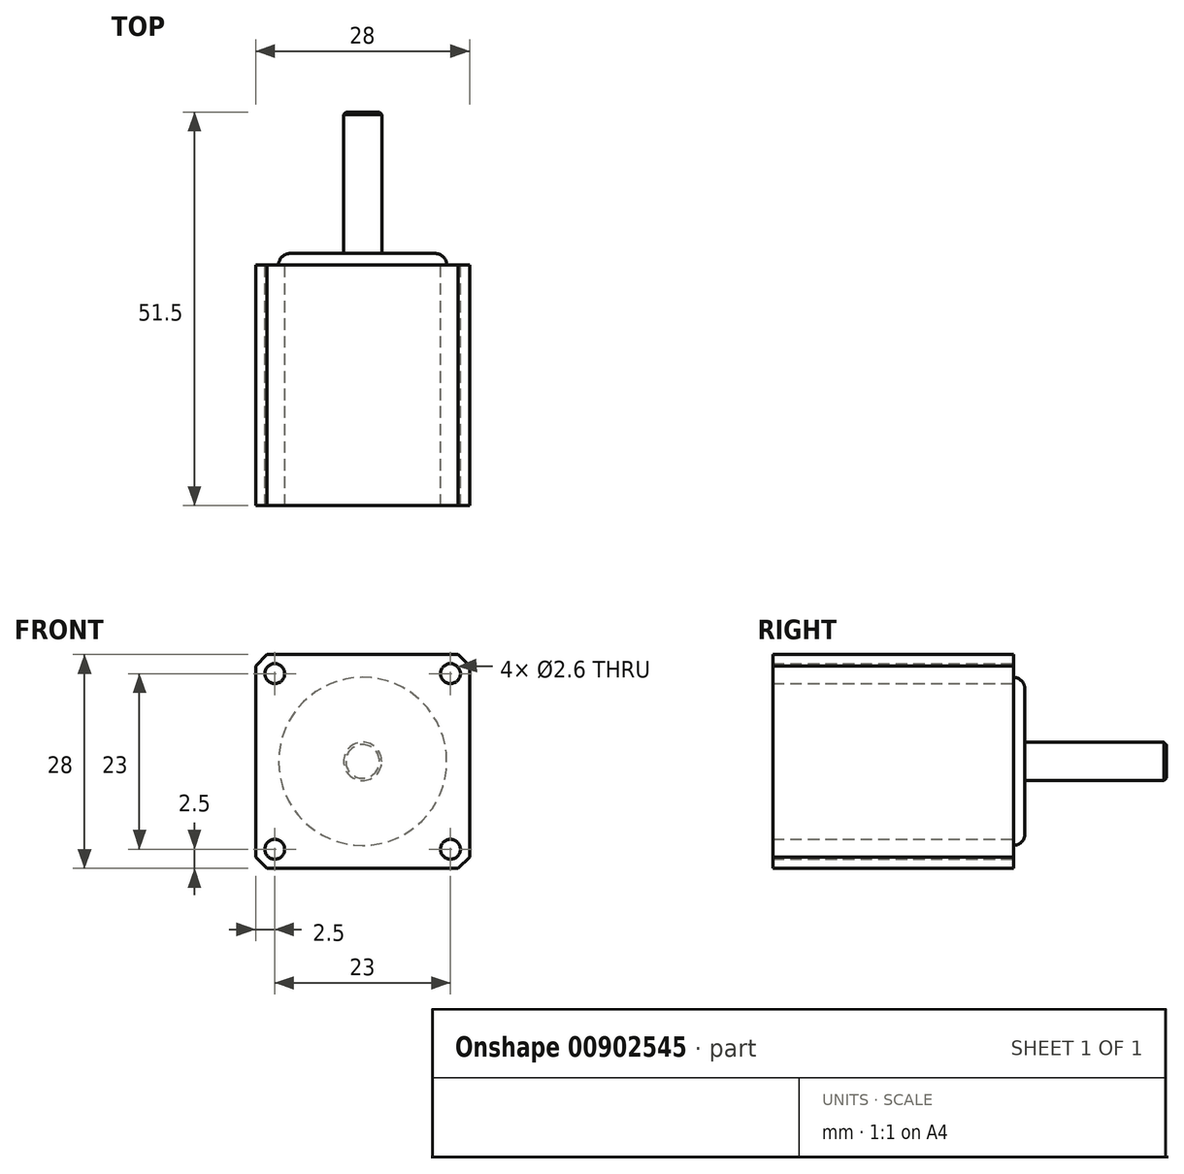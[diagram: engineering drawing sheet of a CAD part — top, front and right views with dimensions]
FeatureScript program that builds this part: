
annotation { "Feature Type Name" : "Feature", "Feature Type Description" : "" }
export const myFeature = defineFeature(function(context is Context, id is Id, definition is map)
    precondition{}
    {
        {
            var Q0;
            Q0=qCreatedBy(makeId("Front.planeOp"),FACE);
            var sketch = newSketch(context, id + "F0", { "sketchPlane" : qUnion([Q0])});
            skPoint(sketch, "E0.middle", {"position": v(0, 0) * mm});
            skLineSegment(sketch, "E1.bottom", {"start": v(14, 14) * mm, "end": v(-14, 14) * mm});
            skLineSegment(sketch, "E1.top", {"start": v(14, -14) * mm, "end": v(-14, -14) * mm});
            skLineSegment(sketch, "E1.left", {"start": v(14, 14) * mm, "end": v(14, -14) * mm});
            skLineSegment(sketch, "E1.right", {"start": v(-14, 14) * mm, "end": v(-14, -14) * mm});
            skSolve(sketch);
        }
        {
            var Q0;
            Q0=makeQuery(id+"F0.imprint","IMPRINT",FACE,{"disambiguationData":[TD([[makeQuery(id+"F0.imprint","IMPRINT",EDGE,{"derivedFrom":sQuery(id+"F0.wireOp",EDGE,"E1.bottom")}),1.0]])]});
            extrude(context, id + "F1", {"entities" : qUnion([Q0]), "oppositeDirection" : true, "depth" : 31.5 * mm, "offsetDistance" : 25 * mm});
        }
        {
            var Q0;
            Q0=makeQuery(id+"F1.opExtrude","CAP_FACE",FACE,{"disambiguationData":[OSD([sQuery(id+"F0.wireOp",EDGE,"E1.bottom"),sQuery(id+"F0.wireOp",EDGE,"E1.top"),sQuery(id+"F0.wireOp",EDGE,"E1.left"),sQuery(id+"F0.wireOp",EDGE,"E1.right")])],"isStart":false});
            var sketch = newSketch(context, id + "F2", { "sketchPlane" : qUnion([Q0])});
            skCircle(sketch, "E2", {"center": v(0, 0) * mm, "radius": 11 * mm});
            skSolve(sketch);
        }
        {
            var Q0;
            Q0=makeQuery(id+"F2.imprint","IMPRINT",FACE,{"disambiguationData":[TD([[makeQuery(id+"F2.imprint","IMPRINT",EDGE,{"derivedFrom":sQuery(id+"F2.wireOp",EDGE,"E2")}),1.0]])]});
            extrude(context, id + "F3", {"entities" : qUnion([Q0]), "operationType" : NewBodyOperationType.ADD, "depth" : 1.5 * mm, "offsetDistance" : 25 * mm});
        }
        {
            var Q0;
            Q0=makeQuery(id+"F3.opExtrude","CAP_FACE",FACE,{"disambiguationData":[OSD([sQuery(id+"F2.wireOp",EDGE,"E2")])],"isStart":false});
            var sketch = newSketch(context, id + "F4", { "sketchPlane" : qUnion([Q0])});
            skCircle(sketch, "E3", {"center": v(0, 0) * mm, "radius": 2.5 * mm});
            skSolve(sketch);
        }
        {
            var Q0;
            Q0=makeQuery(id+"F4.imprint","IMPRINT",FACE,{"disambiguationData":[TD([[makeQuery(id+"F4.imprint","IMPRINT",EDGE,{"derivedFrom":sQuery(id+"F4.wireOp",EDGE,"E3")}),1.0]])]});
            extrude(context, id + "F5", {"entities" : qUnion([Q0]), "operationType" : NewBodyOperationType.ADD, "depth" : 18.5 * mm, "offsetDistance" : 25 * mm});
        }
        {
            var Q0;
            Q0=makeQuery(id+"F1.opExtrude","SWEPT_EDGE",EDGE,{"disambiguationData":[OSD([sQuery(id+"F0.wireOp",EDGE,"E1.bottom"),sQuery(id+"F0.wireOp",EDGE,"E1.left")])]});
            var Q1;
            Q1=makeQuery(id+"F1.opExtrude","SWEPT_EDGE",EDGE,{"disambiguationData":[OSD([sQuery(id+"F0.wireOp",EDGE,"E1.top"),sQuery(id+"F0.wireOp",EDGE,"E1.left")])]});
            var Q2;
            Q2=makeQuery(id+"F1.opExtrude","SWEPT_EDGE",EDGE,{"disambiguationData":[OSD([sQuery(id+"F0.wireOp",EDGE,"E1.top"),sQuery(id+"F0.wireOp",EDGE,"E1.right")])]});
            var Q3;
            Q3=makeQuery(id+"F1.opExtrude","SWEPT_EDGE",EDGE,{"disambiguationData":[OSD([sQuery(id+"F0.wireOp",EDGE,"E1.bottom"),sQuery(id+"F0.wireOp",EDGE,"E1.right")])]});
            chamfer(context, id + "F6", {"entities" : qUnion([Q0, Q1, Q2, Q3]), "width" : 1.5 * mm, "tangentPropagation" : true});
        }
        {
            var Q0;
            Q0=makeQuery(id+"FhSAzgYvToGx3OW_1.opExtrude","CAP_EDGE",EDGE,{"disambiguationData":[OSD([sQuery(id+"F5WzDm25GVoK8AM_1.wireOp",EDGE,"bCLqNWVT-xrID-JnVR-FU4y-eR2KXyvuHUF5")])],"isStart":false});
            var Q1;
            Q1=makeQuery(id+"F5.opExtrude","CAP_EDGE",EDGE,{"disambiguationData":[OSD([sQuery(id+"F4.wireOp",EDGE,"E3")])],"isStart":false});
            chamfer(context, id + "F7", {"entities" : qUnion([Q0, Q1]), "width" : 0.3 * mm, "tangentPropagation" : true});
        }
        {
            var Q0;
            Q0=makeQuery(id+"F3.opExtrude","CAP_EDGE",EDGE,{"disambiguationData":[OSD([sQuery(id+"F2.wireOp",EDGE,"E2")])],"isStart":false});
            fillet(context, id + "F8", {"entities" : qUnion([Q0]), "radius" : 1.5 * mm, "tangentPropagation" : true, "allowEdgeOverflow" : false});
        }
        {
            var Q0;
            Q0=makeQuery(id+"F2.imprint","IMPRINT",FACE,{"disambiguationData":[TD([[makeQuery(id+"F2.imprint","IMPRINT",EDGE,{"derivedFrom":sQuery(id+"F2.wireOp",EDGE,"E2")}),-1.0]])]});
            var sketch = newSketch(context, id + "F9", { "sketchPlane" : qUnion([Q0])});
            skLineSegment(sketch, "E4.bottom", {"start": v(11.5, 11.5) * mm, "end": v(-11.5, 11.5) * mm});
            skLineSegment(sketch, "E4.top", {"start": v(11.5, -11.5) * mm, "end": v(-11.5, -11.5) * mm});
            skLineSegment(sketch, "E4.left", {"start": v(11.5, 11.5) * mm, "end": v(11.5, -11.5) * mm});
            skLineSegment(sketch, "E4.right", {"start": v(-11.5, 11.5) * mm, "end": v(-11.5, -11.5) * mm});
            skPoint(sketch, "E4.middle", {"position": v(0, 0) * mm});
            skCircle(sketch, "E5", {"center": v(-11.5, 11.5) * mm, "radius": 1.3 * mm});
            skCircle(sketch, "E6", {"center": v(-11.5, -11.5) * mm, "radius": 1.3 * mm});
            skCircle(sketch, "E7", {"center": v(11.5, -11.5) * mm, "radius": 1.3 * mm});
            skCircle(sketch, "E8", {"center": v(11.5, 11.5) * mm, "radius": 1.3 * mm});
            skSolve(sketch);
        }
        {
            var Q0;
            {var subQ0=sQuery(id+"F9.wireOp",EDGE,"E4.right");var subQ1=sQuery(id+"F9.wireOp",EDGE,"E4.top");var subQ2=makeQuery(id+"F9.imprint","INTERSECT",VERTEX,{"derivedFrom":[subQ1,subQ0]});Q0=makeQuery(id+"F9.imprint","IMPRINT",FACE,{"disambiguationData":[TD([[makeQuery(id+"F9.imprint","IMPRINT",EDGE,{"disambiguationData":[TD([[subQ2,1.0]])],"derivedFrom":subQ1}),1.0]])]});}
            var Q1;
            {var subQ0=sQuery(id+"F9.wireOp",EDGE,"E4.right");var subQ1=sQuery(id+"F9.wireOp",EDGE,"E4.top");var subQ2=makeQuery(id+"F9.imprint","INTERSECT",VERTEX,{"derivedFrom":[subQ1,subQ0]});Q1=makeQuery(id+"F9.imprint","IMPRINT",FACE,{"disambiguationData":[TD([[makeQuery(id+"F9.imprint","IMPRINT",EDGE,{"disambiguationData":[TD([[subQ2,1.0]])],"derivedFrom":subQ1}),-1.0]])]});}
            var Q2;
            {var subQ0=sQuery(id+"F9.wireOp",EDGE,"E4.left");var subQ1=sQuery(id+"F9.wireOp",EDGE,"E4.top");var subQ2=makeQuery(id+"F9.imprint","INTERSECT",VERTEX,{"derivedFrom":[subQ1,subQ0]});Q2=makeQuery(id+"F9.imprint","IMPRINT",FACE,{"disambiguationData":[TD([[makeQuery(id+"F9.imprint","IMPRINT",EDGE,{"disambiguationData":[TD([[subQ2,-1.0]])],"derivedFrom":subQ1}),1.0]])]});}
            var Q3;
            {var subQ0=sQuery(id+"F9.wireOp",EDGE,"E4.left");var subQ1=sQuery(id+"F9.wireOp",EDGE,"E4.top");var subQ2=makeQuery(id+"F9.imprint","INTERSECT",VERTEX,{"derivedFrom":[subQ1,subQ0]});Q3=makeQuery(id+"F9.imprint","IMPRINT",FACE,{"disambiguationData":[TD([[makeQuery(id+"F9.imprint","IMPRINT",EDGE,{"disambiguationData":[TD([[subQ2,-1.0]])],"derivedFrom":subQ1}),-1.0]])]});}
            var Q4;
            {var subQ0=sQuery(id+"F9.wireOp",EDGE,"E4.left");var subQ1=sQuery(id+"F9.wireOp",EDGE,"E4.bottom");var subQ2=makeQuery(id+"F9.imprint","INTERSECT",VERTEX,{"derivedFrom":[subQ1,subQ0]});Q4=makeQuery(id+"F9.imprint","IMPRINT",FACE,{"disambiguationData":[TD([[makeQuery(id+"F9.imprint","IMPRINT",EDGE,{"disambiguationData":[TD([[subQ2,-1.0]])],"derivedFrom":subQ1}),1.0]])]});}
            var Q5;
            {var subQ0=sQuery(id+"F9.wireOp",EDGE,"E4.left");var subQ1=sQuery(id+"F9.wireOp",EDGE,"E4.bottom");var subQ2=makeQuery(id+"F9.imprint","INTERSECT",VERTEX,{"derivedFrom":[subQ1,subQ0]});Q5=makeQuery(id+"F9.imprint","IMPRINT",FACE,{"disambiguationData":[TD([[makeQuery(id+"F9.imprint","IMPRINT",EDGE,{"disambiguationData":[TD([[subQ2,-1.0]])],"derivedFrom":subQ1}),-1.0]])]});}
            var Q6;
            {var subQ0=sQuery(id+"F9.wireOp",EDGE,"E4.right");var subQ1=sQuery(id+"F9.wireOp",EDGE,"E4.bottom");var subQ2=makeQuery(id+"F9.imprint","INTERSECT",VERTEX,{"derivedFrom":[subQ1,subQ0]});Q6=makeQuery(id+"F9.imprint","IMPRINT",FACE,{"disambiguationData":[TD([[makeQuery(id+"F9.imprint","IMPRINT",EDGE,{"disambiguationData":[TD([[subQ2,1.0]])],"derivedFrom":subQ1}),1.0]])]});}
            var Q7;
            {var subQ0=sQuery(id+"F9.wireOp",EDGE,"E4.right");var subQ1=sQuery(id+"F9.wireOp",EDGE,"E4.bottom");var subQ2=makeQuery(id+"F9.imprint","INTERSECT",VERTEX,{"derivedFrom":[subQ1,subQ0]});Q7=makeQuery(id+"F9.imprint","IMPRINT",FACE,{"disambiguationData":[TD([[makeQuery(id+"F9.imprint","IMPRINT",EDGE,{"disambiguationData":[TD([[subQ2,1.0]])],"derivedFrom":subQ1}),-1.0]])]});}
            extrude(context, id + "F10", {"entities" : qUnion([Q0, Q1, Q2, Q3, Q4, Q5, Q6, Q7]), "operationType" : NewBodyOperationType.REMOVE, "oppositeDirection" : true, "depth" : 31.5 * mm, "offsetDistance" : 25 * mm});
        }
    });
